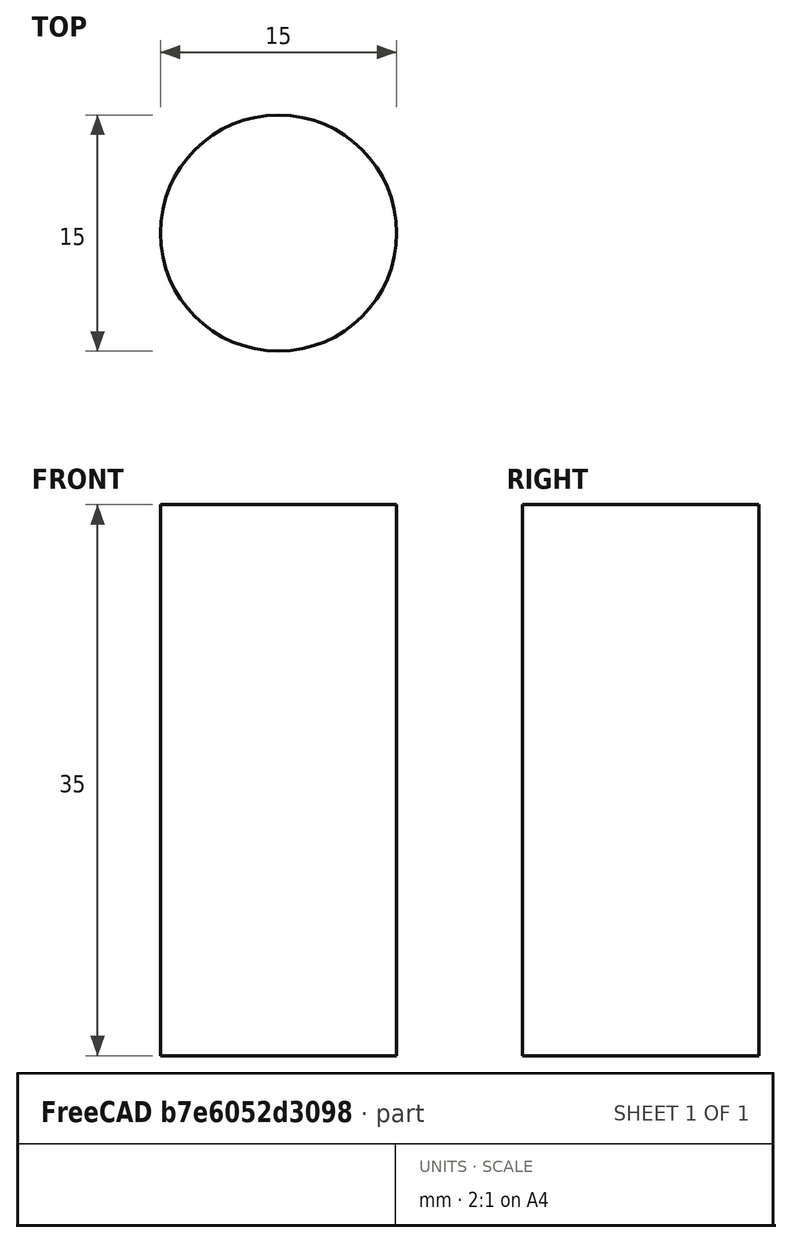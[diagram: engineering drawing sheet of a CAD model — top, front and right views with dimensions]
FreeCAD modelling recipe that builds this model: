
FCSTD DOCUMENT  (FreeCAD 0.18R4 (GitTag))
Label: armAxle
License: All rights reserved
LicenseURL: http://en.wikipedia.org/wiki/All_rights_reserved
objects: Sketcher::SketchObject×1, PartDesign::Pad×1, PartDesign::Body×1, App::Part×1, Part::Feature×1
note: 5 computed .brp shape members not serialized (recipe doc carries the construction recipe); baked Part::Feature solids carry a one-line shape summary decoded from their .brp

FEATURE [Sketcher::SketchObject] Sketch
  MapMode = 5
  Support = -> [XY_Plane001]
  sketch-geometry (1):
    g0: Circle CenterX=0 CenterY=0 CenterZ=0 NormalX=0 NormalY=0 NormalZ=1 AngleXU=0 Radius=7.5
  constraints (2):
    c: Diameter(g0) = 15
    c: Coincident(g-1,g0)
FEATURE [PartDesign::Pad] Pad
  Length = 35
  Length2 = 100
  Profile = -> Sketch
  Type = 0
FEATURE [PartDesign::Body] Body  label="armAxle"
  Group = -> [Sketch,Pad]
  Origin = -> Origin001
  Tip = -> Pad
FEATURE [App::Part] Part
  Group = -> [Body]
  Origin = -> Origin
FEATURE [Part::Feature] Pad001  label="Robot_ArmAxle"
  shape: bbox 15 x 15 x 35 mm, 3 faces (baked)
